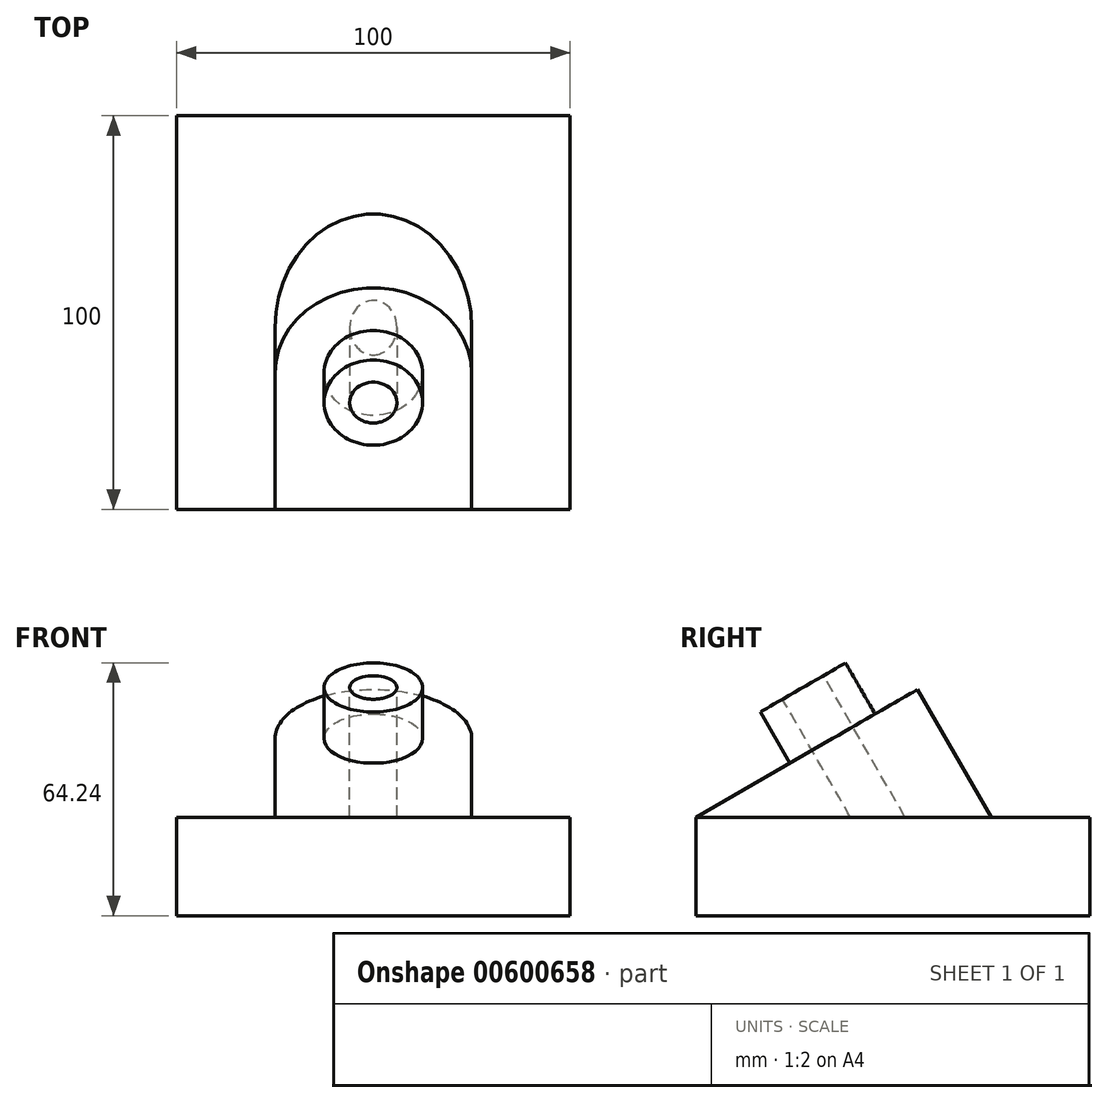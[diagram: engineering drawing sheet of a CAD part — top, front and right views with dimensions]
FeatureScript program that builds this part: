
annotation { "Feature Type Name" : "Feature", "Feature Type Description" : "" }
export const myFeature = defineFeature(function(context is Context, id is Id, definition is map)
    precondition{}
    {
        {
            var Q0;
            Q0=qCreatedBy(makeId("Top.planeOp"),FACE);
            var sketch = newSketch(context, id + "F0", { "sketchPlane" : qUnion([Q0])});
            skLineSegment(sketch, "E0.bottom", {"start": v(0, 0) * mm, "end": v(100, 0) * mm});
            skLineSegment(sketch, "E0.top", {"start": v(0, 100) * mm, "end": v(100, 100) * mm});
            skLineSegment(sketch, "E0.left", {"start": v(0, 0) * mm, "end": v(0, 100) * mm});
            skLineSegment(sketch, "E0.right", {"start": v(100, 0) * mm, "end": v(100, 100) * mm});
            skSolve(sketch);
        }
        {
            var Q0;
            Q0 = qSketchRegion(id + "F0", true);
            extrude(context, id + "F1", {"entities" : qUnion([Q0]), "depth" : 25 * mm, "offsetDistance" : 25 * mm});
        }
        {
            var Q0;
            Q0=makeQuery(id+"F1.opExtrude","CAP_EDGE",EDGE,{"disambiguationData":[OSD([sQuery(id+"F0.wireOp",EDGE,"E0.bottom")])],"isStart":false});
            cPlane(context, id + "F2", {"entities" : qUnion([Q0]), "cplaneType" : CPlaneType.LINE_ANGLE, "offset" : 25 * mm, "angle" : 60 * degree, "oppositeDirection" : true, "width" : 150 * mm, "height" : 150 * mm});
        }
        {
            var Q0;
            Q0=qCreatedBy(id+"F2.planeOp",FACE);
            var sketch = newSketch(context, id + "F3", { "sketchPlane" : qUnion([Q0])});
            skLineSegment(sketch, "E1", {"start": v(25, -12.5) * mm, "end": v(25, -52.5) * mm});
            skLineSegment(sketch, "E2", {"start": v(75, -52.5) * mm, "end": v(75, -12.5) * mm});
            skLineSegment(sketch, "E3", {"start": v(75, -12.5) * mm, "end": v(25, -12.5) * mm});
            skArc(sketch, "E4", {"start": v(25, -52.5) * mm, "mid": v(50, -77.5) * mm, "end": v(75, -52.5) * mm});
            skSolve(sketch);
        }
        {
            var Q0;
            Q0 = qSketchRegion(id + "F3", true);
            extrude(context, id + "F4", {"entities" : qUnion([Q0]), "operationType" : NewBodyOperationType.ADD, "endBound" : BoundingType.UP_TO_NEXT, "depth" : 25 * mm, "offsetDistance" : 25 * mm});
        }
        {
            var Q0;
            Q0=makeQuery(id+"F4.opExtrude","CAP_FACE",FACE,{"disambiguationData":[OSD([sQuery(id+"F3.wireOp",EDGE,"E1"),sQuery(id+"F3.wireOp",EDGE,"E2"),sQuery(id+"F3.wireOp",EDGE,"E3"),sQuery(id+"F3.wireOp",EDGE,"E4")])],"isStart":true});
            var sketch = newSketch(context, id + "F5", { "sketchPlane" : qUnion([Q0])});
            skCircle(sketch, "E5", {"center": v(50, 52.5) * mm, "radius": 12.5 * mm});
            skSolve(sketch);
        }
        {
            var Q0;
            Q0 = qSketchRegion(id + "F5", true);
            extrude(context, id + "F6", {"entities" : qUnion([Q0]), "operationType" : NewBodyOperationType.ADD, "depth" : 15 * mm, "offsetDistance" : 25 * mm});
        }
        {
            var Q0;
            Q0=makeQuery(id+"F6.opExtrude","CAP_FACE",FACE,{"disambiguationData":[OSD([sQuery(id+"F5.wireOp",EDGE,"E5")])],"isStart":false});
            var sketch = newSketch(context, id + "F7", { "sketchPlane" : qUnion([Q0])});
            skCircle(sketch, "E6", {"center": v(50, 52.5) * mm, "radius": 6 * mm});
            skSolve(sketch);
        }
        {
            var Q0;
            Q0 = qSketchRegion(id + "F7", true);
            var Q1;
            Q1=makeQuery(id+"F1.opExtrude","CAP_FACE",FACE,{"disambiguationData":[OSD([sQuery(id+"F0.wireOp",EDGE,"E0.bottom"),sQuery(id+"F0.wireOp",EDGE,"E0.top"),sQuery(id+"F0.wireOp",EDGE,"E0.left"),sQuery(id+"F0.wireOp",EDGE,"E0.right")])],"isStart":false});
            extrude(context, id + "F8", {"entities" : qUnion([Q0]), "operationType" : NewBodyOperationType.REMOVE, "endBound" : BoundingType.UP_TO_SURFACE, "oppositeDirection" : true, "depth" : 25 * mm, "endBoundEntityFace" : qUnion([Q1]), "offsetDistance" : 25 * mm});
        }
    });
